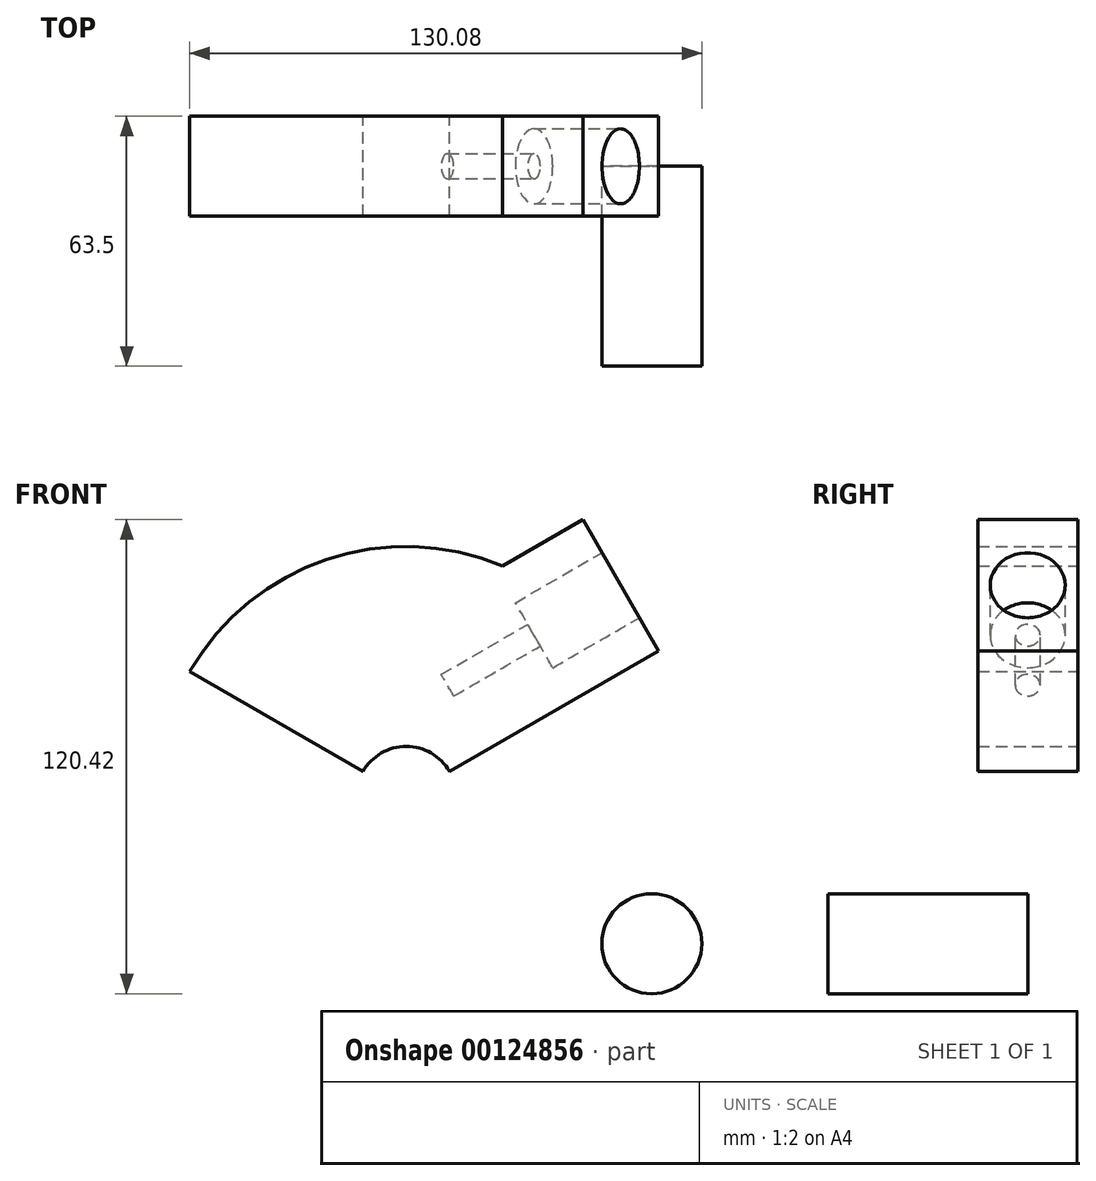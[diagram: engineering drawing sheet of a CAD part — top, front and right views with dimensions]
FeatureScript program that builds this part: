
annotation { "Feature Type Name" : "Feature", "Feature Type Description" : "" }
export const myFeature = defineFeature(function(context is Context, id is Id, definition is map)
    precondition{}
    {
        {
            var Q0;
            Q0=qCreatedBy(makeId("Front.planeOp"),FACE);
            var sketch = newSketch(context, id + "F0", { "sketchPlane" : qUnion([Q0])});
            skArc(sketch, "E0", {"start": v(11, 6.35) * mm, "mid": v(0, 12.7) * mm, "end": v(-11, 6.35) * mm});
            skArc(sketch, "E1", {"start": v(55, 31.75) * mm, "mid": v(0, 63.5) * mm, "end": v(-55, 31.75) * mm});
            skLineSegment(sketch, "E2", {"start": v(11, 6.35) * mm, "end": v(64.09, 37) * mm});
            skLineSegment(sketch, "E3", {"start": v(64.09, 37) * mm, "end": v(44.86, 70.31) * mm});
            skLineSegment(sketch, "E4", {"start": v(44.86, 70.31) * mm, "end": v(24.53, 58.57) * mm});
            skLineSegment(sketch, "E5", {"start": v(-11, 6.35) * mm, "end": v(-55, 31.75) * mm});
            skSolve(sketch);
        }
        {
            var Q0;
            Q0 = qSketchRegion(id + "F0", true);
            var Q1;
            {var subQ1=sQuery(id+"F0.wireOp",EDGE,"E0");Q1=makeQuery(id+"F0.imprint","IMPRINT",FACE,{"disambiguationData":[TD([[makeQuery(id+"F0.imprint","IMPRINT",EDGE,{"derivedFrom":subQ1}),-1.0]])]});}
            extrude(context, id + "F1", {"entities" : qUnion([Q0, Q1]), "endBound" : BoundingType.SYMMETRIC, "depth" : 25.4 * mm});
        }
        {
            var Q0;
            Q0=makeQuery(id+"F1.opExtrude","SWEPT_FACE",FACE,{"disambiguationData":[OSD([sQuery(id+"F0.wireOp",EDGE,"E3")])]});
            var sketch = newSketch(context, id + "F2", { "sketchPlane" : qUnion([Q0])});
            skCircle(sketch, "E6", {"center": v(0, 19.23) * mm, "radius": 9.53 * mm});
            skPoint(sketch, "E6.centerSnap0", {"position": v(12.7, 19.23) * mm});
            skCircle(sketch, "E7", {"center": v(0, 19.23) * mm, "radius": 3.18 * mm});
            skSolve(sketch);
        }
        {
            var Q0;
            Q0=makeQuery(id+"F2.imprint","IMPRINT",FACE,{"disambiguationData":[TD([[makeQuery(id+"F2.imprint","IMPRINT",EDGE,{"derivedFrom":sQuery(id+"F2.wireOp",EDGE,"E7")}),1.0]])]});
            extrude(context, id + "F3", {"entities" : qUnion([Q0]), "operationType" : NewBodyOperationType.REMOVE, "oppositeDirection" : true, "depth" : 50.8 * mm});
        }
        {
            var Q0;
            Q0=makeQuery(id+"F2.imprint","IMPRINT",FACE,{"disambiguationData":[TD([[makeQuery(id+"F2.imprint","IMPRINT",EDGE,{"derivedFrom":sQuery(id+"F2.wireOp",EDGE,"E6")}),1.0]])]});
            extrude(context, id + "F4", {"entities" : qUnion([Q0]), "operationType" : NewBodyOperationType.REMOVE, "oppositeDirection" : true, "depth" : 25.4 * mm});
        }
        {
            var Q0;
            Q0=qCreatedBy(makeId("Front.planeOp"),FACE);
            var sketch = newSketch(context, id + "F5", { "sketchPlane" : qUnion([Q0])});
            skCircle(sketch, "E8", {"center": v(62.39, -37.41) * mm, "radius": 12.7 * mm});
            skSolve(sketch);
        }
        {
            var Q0;
            Q0 = qSketchRegion(id + "F5", true);
            extrude(context, id + "F6", {"entities" : qUnion([Q0]), "depth" : 50.8 * mm});
        }
    });
